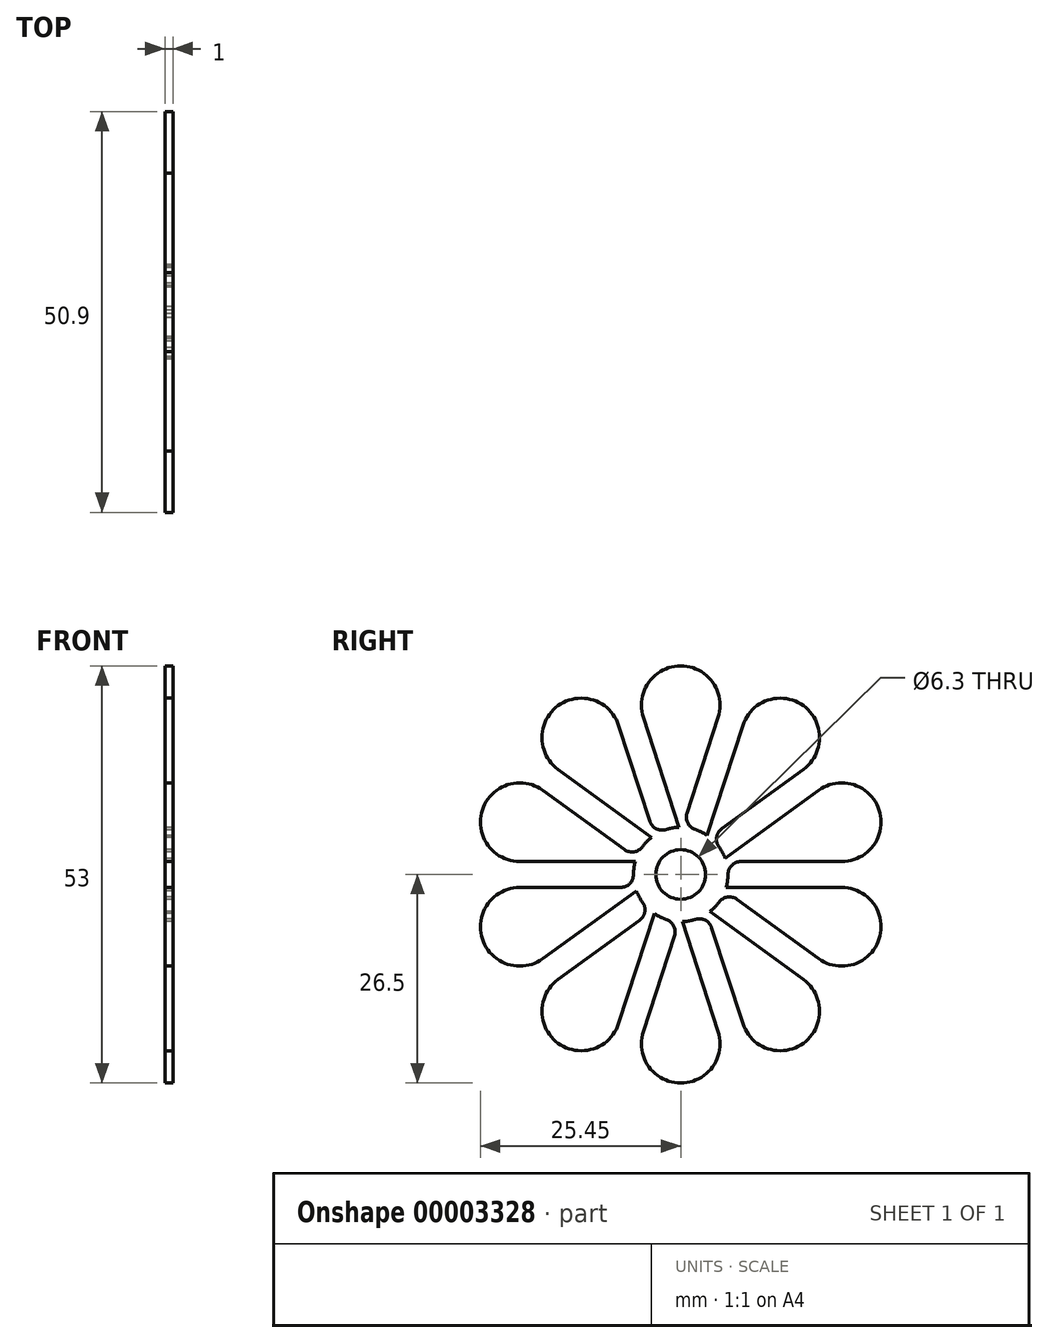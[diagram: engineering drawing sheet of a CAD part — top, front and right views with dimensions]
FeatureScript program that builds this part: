
annotation { "Feature Type Name" : "Feature", "Feature Type Description" : "" }
export const myFeature = defineFeature(function(context is Context, id is Id, definition is map)
    precondition{}
    {
        {
            var Q0;
            Q0=qCreatedBy(makeId("Right.planeOp"),FACE);
            var sketch = newSketch(context, id + "F0", { "sketchPlane" : qUnion([Q0])});
            skCircle(sketch, "E0", {"center": v(0, 0) * mm, "radius": 3.15 * mm});
            skCircle(sketch, "E1", {"center": v(0, 0) * mm, "radius": 21.5 * mm, "construction": true});
            skCircle(sketch, "E2", {"center": v(0, 21.5) * mm, "radius": 5 * mm});
            skCircle(sketch, "E3", {"center": v(12.64, 17.4) * mm, "radius": 5 * mm, "construction": true});
            skLineSegment(sketch, "E4", {"start": v(0, 0) * mm, "end": v(0, 21.5) * mm, "construction": true});
            skLineSegment(sketch, "E5", {"start": v(0, 0) * mm, "end": v(12.64, 17.4) * mm, "construction": true});
            skLineSegment(sketch, "E6", {"start": v(4.76, 19.95) * mm, "end": v(-1.56, 0.5) * mm});
            skLineSegment(sketch, "E7", {"start": v(7.88, 18.94) * mm, "end": v(1.56, -0.5) * mm, "construction": true});
            skLineSegment(sketch, "E8", {"start": v(1.56, -0.5) * mm, "end": v(-1.56, 0.5) * mm, "construction": true});
            skCircle(sketch, "E9", {"center": v(0, 0) * mm, "radius": 6 * mm});
            skArc(sketch, "E10", {"start": v(0.8, 7.78) * mm, "mid": v(0.9, 6.52) * mm, "end": v(1.85, 5.7) * mm});
            skLineSegment(sketch, "E11.0.MirrorCS", {"start": v(-4.76, 19.95) * mm, "end": v(1.56, 0.5) * mm});
            skArc(sketch, "E12.0.MirrorCS", {"start": v(-0.8, 7.78) * mm, "mid": v(-0.9, 6.52) * mm, "end": v(-1.85, 5.7) * mm});
            skSolve(sketch);
        }
        {
            var Q0;
            {var subQ0=sQuery(id+"F0.wireOp",EDGE,"E2");var subQ2=makeQuery(id+"F0.imprint","INTERSECT",VERTEX,{"derivedFrom":[subQ0,sQuery(id+"F0.wireOp",EDGE,"E6")]});Q0=makeQuery(id+"F0.imprint","IMPRINT",FACE,{"disambiguationData":[TD([[makeQuery(id+"F0.imprint","IMPRINT",EDGE,{"disambiguationData":[TD([[subQ2,1.0]])],"derivedFrom":subQ0}),1.0]])]});}
            var Q1;
            {var subQ4=sQuery(id+"F0.wireOp",EDGE,"E2");var subQ6=sQuery(id+"F0.wireOp",EDGE,"E6");var subQ9=makeQuery(id+"F0.imprint","INTERSECT",VERTEX,{"derivedFrom":[subQ4,subQ6]});Q1=makeQuery(id+"F0.imprint","IMPRINT",FACE,{"disambiguationData":[TD([[makeQuery(id+"F0.imprint","IMPRINT",EDGE,{"disambiguationData":[TD([[subQ9,1.0]])],"derivedFrom":subQ4}),-1.0]])]});}
            var Q2;
            {var subQ0=sQuery(id+"F0.wireOp",EDGE,"E10");Q2=makeQuery(id+"F0.imprint","IMPRINT",FACE,{"disambiguationData":[TD([[makeQuery(id+"F0.imprint","IMPRINT",EDGE,{"derivedFrom":subQ0}),-1.0]])]});}
            var Q3;
            {var subQ0=sQuery(id+"F0.wireOp",EDGE,"E12.0.MirrorCS");Q3=makeQuery(id+"F0.imprint","IMPRINT",FACE,{"disambiguationData":[TD([[makeQuery(id+"F0.imprint","IMPRINT",EDGE,{"derivedFrom":subQ0}),1.0]])]});}
            extrude(context, id + "F1", {"entities" : qUnion([Q0, Q1, Q2, Q3]), "depth" : 1 * mm});
        }
        {
            var Q0;
            Q0=makeQuery(id+"F1.opExtrude","SWEPT_FACE",FACE,{"disambiguationData":[OSD([sQuery(id+"F0.wireOp",EDGE,"E12.0.MirrorCS")])]});
            var Q1;
            Q1=makeQuery(id+"F1.opExtrude","SWEPT_FACE",FACE,{"disambiguationData":[OSD([sQuery(id+"F0.wireOp",EDGE,"E11.0.MirrorCS")])]});
            var Q2;
            Q2=makeQuery(id+"F1.opExtrude","SWEPT_FACE",FACE,{"disambiguationData":[OSD([sQuery(id+"F0.wireOp",EDGE,"E2")])]});
            var Q3;
            Q3=makeQuery(id+"F1.opExtrude","SWEPT_FACE",FACE,{"disambiguationData":[OSD([sQuery(id+"F0.wireOp",EDGE,"E6")])]});
            var Q4;
            Q4=makeQuery(id+"F1.opExtrude","SWEPT_FACE",FACE,{"disambiguationData":[OSD([sQuery(id+"F0.wireOp",EDGE,"E10")])]});
            var Q5;
            Q5=makeQuery(id+"F1.opExtrude","SWEPT_BODY",BODY,{"disambiguationData":[OSD([sQuery(id+"F0.wireOp",EDGE,"E2"),sQuery(id+"F0.wireOp",EDGE,"E6"),sQuery(id+"F0.wireOp",EDGE,"E9"),sQuery(id+"F0.wireOp",EDGE,"E10"),sQuery(id+"F0.wireOp",EDGE,"E11.0.MirrorCS"),sQuery(id+"F0.wireOp",EDGE,"E12.0.MirrorCS")])]});
            var Q6;
            Q6=makeQuery(id+"F1.opExtrude","CAP_EDGE",EDGE,{"disambiguationData":[OSD([sQuery(id+"F0.wireOp",EDGE,"E9")])],"isStart":true});
            circularPattern(context, id + "F2", {"entities" : qUnion([Q5]), "axis" : qUnion([Q6]), "angle" : 36 * degree, "instanceCount" : 10});
        }
        {
            var Q0;
            {var subQ1=sQuery(id+"F0.wireOp",EDGE,"E6");var subQ3=sQuery(id+"F0.wireOp",EDGE,"E0");var subQ10=makeQuery(id+"F0.imprint","INTERSECT",VERTEX,{"derivedFrom":[subQ3,subQ1]});Q0=makeQuery(id+"F0.imprint","IMPRINT",FACE,{"disambiguationData":[TD([[makeQuery(id+"F0.imprint","IMPRINT",EDGE,{"disambiguationData":[TD([[subQ10,-1.0]])],"derivedFrom":subQ3}),-1.0]])]});}
            var Q1;
            {var subQ1=sQuery(id+"F0.wireOp",EDGE,"E6");var subQ3=sQuery(id+"F0.wireOp",EDGE,"E0");var subQ5=makeQuery(id+"F0.imprint","INTERSECT",VERTEX,{"derivedFrom":[subQ3,subQ1]});Q1=makeQuery(id+"F0.imprint","IMPRINT",FACE,{"disambiguationData":[TD([[makeQuery(id+"F0.imprint","IMPRINT",EDGE,{"disambiguationData":[TD([[subQ5,1.0]])],"derivedFrom":subQ3}),-1.0]])]});}
            var Q2;
            {var subQ0=sQuery(id+"F0.wireOp",EDGE,"E11.0.MirrorCS");var subQ3=sQuery(id+"F0.wireOp",EDGE,"E6");var subQ4=makeQuery(id+"F0.imprint","INTERSECT",VERTEX,{"derivedFrom":[subQ3,subQ0]});Q2=makeQuery(id+"F0.imprint","IMPRINT",FACE,{"disambiguationData":[TD([[makeQuery(id+"F0.imprint","IMPRINT",EDGE,{"disambiguationData":[TD([[subQ4,1.0]])],"derivedFrom":subQ3}),-1.0]])]});}
            extrude(context, id + "F3", {"entities" : qUnion([Q0, Q1, Q2]), "operationType" : NewBodyOperationType.ADD, "depth" : 1 * mm});
        }
    });
